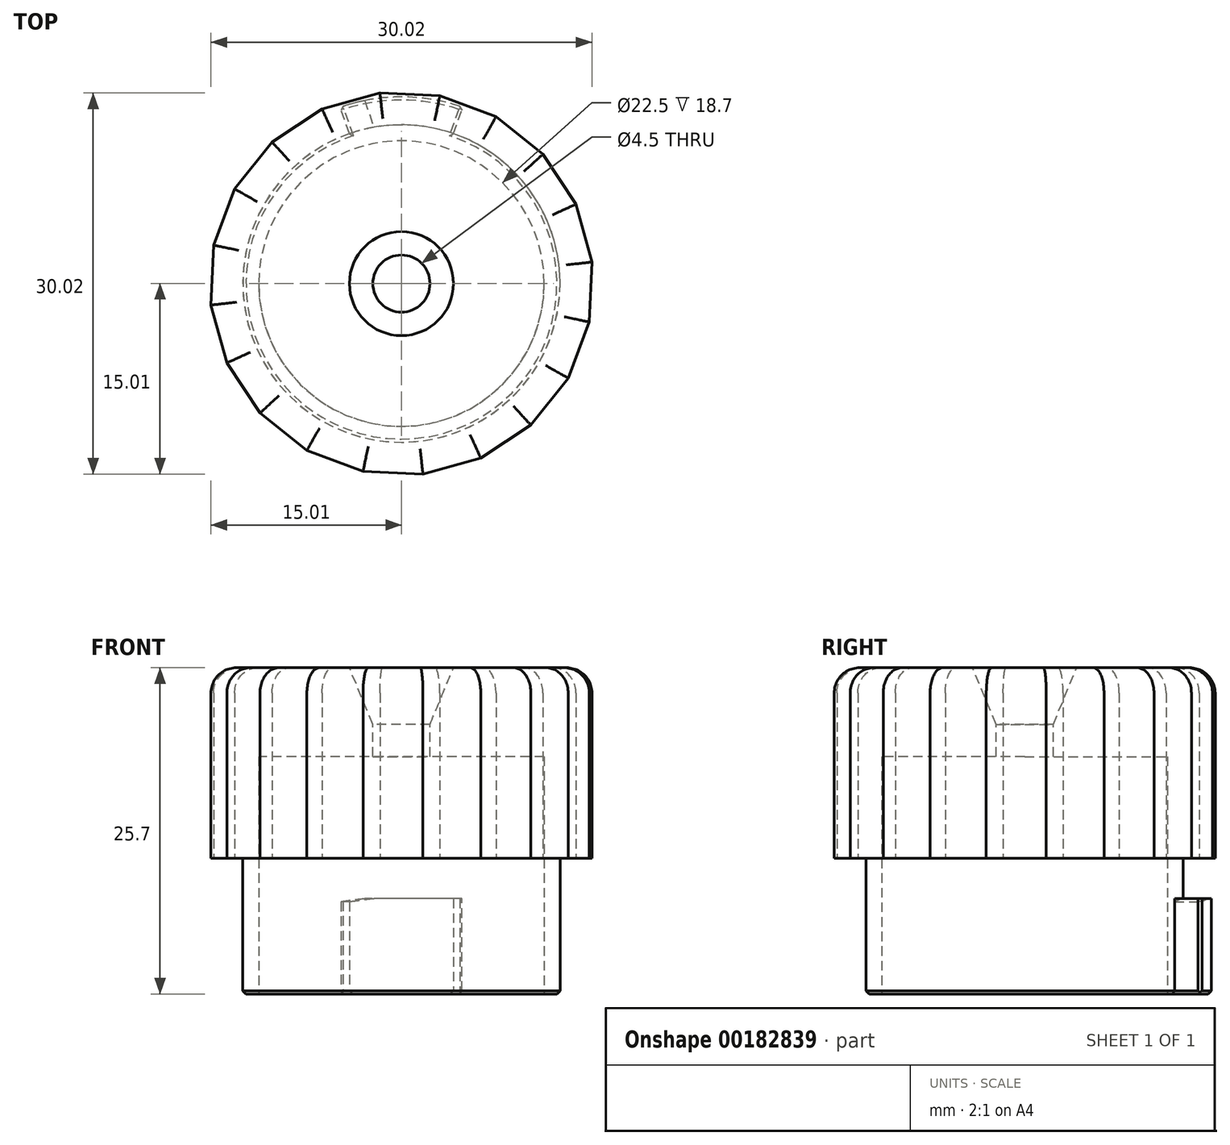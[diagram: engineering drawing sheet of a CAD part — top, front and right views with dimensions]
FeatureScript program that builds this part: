
annotation { "Feature Type Name" : "Feature", "Feature Type Description" : "" }
export const myFeature = defineFeature(function(context is Context, id is Id, definition is map)
    precondition{}
    {
        {
            var Q0;
            Q0=qCreatedBy(makeId("Top.planeOp"),FACE);
            var sketch = newSketch(context, id + "F0", { "sketchPlane" : qUnion([Q0])});
            skLineSegment(sketch, "E0", {"start": v(-4.83, 13.88) * mm, "end": v(-4.1, 11.8) * mm});
            skLineSegment(sketch, "E1", {"start": v(4.83, 13.88) * mm, "end": v(4.1, 11.8) * mm});
            skArc(sketch, "E2", {"start": v(-4.1, 11.8) * mm, "mid": v(0, -12.5) * mm, "end": v(4.1, 11.8) * mm});
            skArc(sketch, "E3", {"start": v(4.83, 13.88) * mm, "mid": v(0, 14.7) * mm, "end": v(-4.83, 13.88) * mm});
            skSolve(sketch);
        }
        {
            var Q0;
            Q0=makeQuery(id+"F0.imprint","IMPRINT",FACE,{"disambiguationData":[TD([[makeQuery(id+"F0.imprint","IMPRINT",EDGE,{"derivedFrom":sQuery(id+"F0.wireOp",EDGE,"E0")}),1.0]])]});
            extrude(context, id + "F1", {"entities" : qUnion([Q0]), "depth" : 7.5 * mm});
        }
        {
            var Q0;
            Q0=makeQuery(id+"F1.opExtrude","CAP_FACE",FACE,{"disambiguationData":[OSD([sQuery(id+"F0.wireOp",EDGE,"E0"),sQuery(id+"F0.wireOp",EDGE,"E1"),sQuery(id+"F0.wireOp",EDGE,"E2"),sQuery(id+"F0.wireOp",EDGE,"E3")])],"isStart":false});
            var sketch = newSketch(context, id + "F2", { "sketchPlane" : qUnion([Q0])});
            skCircle(sketch, "E4", {"center": v(0, 0) * mm, "radius": 12.5 * mm});
            skSolve(sketch);
        }
        {
            var Q0;
            Q0 = qSketchRegion(id + "F2", true);
            extrude(context, id + "F3", {"entities" : qUnion([Q0]), "operationType" : NewBodyOperationType.ADD, "depth" : 3.2 * mm});
        }
        {
            var Q0;
            Q0=makeQuery(id+"F3.opExtrude","CAP_FACE",FACE,{"disambiguationData":[OSD([sQuery(id+"F2.wireOp",EDGE,"E4")])],"isStart":false});
            var sketch = newSketch(context, id + "F4", { "sketchPlane" : qUnion([Q0])});
            skCircle(sketch, "E5.cCircle", {"center": v(0, 0) * mm, "radius": 14.92 * mm, "construction": true});
            skLineSegment(sketch, "E5.0", {"start": v(11.15, 10.2) * mm, "end": v(13.75, 6.25) * mm});
            skLineSegment(sketch, "E5.1", {"start": v(13.75, 6.25) * mm, "end": v(15.01, 1.7) * mm});
            skLineSegment(sketch, "E5.2", {"start": v(15.01, 1.7) * mm, "end": v(14.8, -3.03) * mm});
            skLineSegment(sketch, "E5.3", {"start": v(14.8, -3.03) * mm, "end": v(13.14, -7.45) * mm});
            skLineSegment(sketch, "E5.4", {"start": v(13.14, -7.45) * mm, "end": v(10.2, -11.15) * mm});
            skLineSegment(sketch, "E5.5", {"start": v(10.2, -11.15) * mm, "end": v(6.25, -13.75) * mm});
            skLineSegment(sketch, "E5.6", {"start": v(6.25, -13.75) * mm, "end": v(1.7, -15.01) * mm});
            skLineSegment(sketch, "E5.7", {"start": v(1.7, -15.01) * mm, "end": v(-3.03, -14.8) * mm});
            skLineSegment(sketch, "E5.8", {"start": v(-3.03, -14.8) * mm, "end": v(-7.45, -13.14) * mm});
            skLineSegment(sketch, "E5.9", {"start": v(-7.45, -13.14) * mm, "end": v(-11.15, -10.2) * mm});
            skLineSegment(sketch, "E5.10", {"start": v(-11.15, -10.2) * mm, "end": v(-13.75, -6.25) * mm});
            skLineSegment(sketch, "E5.11", {"start": v(-13.75, -6.25) * mm, "end": v(-15.01, -1.7) * mm});
            skLineSegment(sketch, "E5.12", {"start": v(-15.01, -1.7) * mm, "end": v(-14.8, 3.03) * mm});
            skLineSegment(sketch, "E5.13", {"start": v(-14.8, 3.03) * mm, "end": v(-13.14, 7.45) * mm});
            skLineSegment(sketch, "E5.14", {"start": v(-13.14, 7.45) * mm, "end": v(-10.2, 11.15) * mm});
            skLineSegment(sketch, "E5.15", {"start": v(-10.2, 11.15) * mm, "end": v(-6.25, 13.75) * mm});
            skLineSegment(sketch, "E5.16", {"start": v(-6.25, 13.75) * mm, "end": v(-1.7, 15.01) * mm});
            skLineSegment(sketch, "E5.17", {"start": v(-1.7, 15.01) * mm, "end": v(3.03, 14.8) * mm});
            skLineSegment(sketch, "E5.18", {"start": v(3.03, 14.8) * mm, "end": v(7.45, 13.14) * mm});
            skLineSegment(sketch, "E5.19", {"start": v(7.45, 13.14) * mm, "end": v(11.15, 10.2) * mm});
            skPoint(sketch, "E5.0.midPoint", {"position": v(12.45, 8.22) * mm});
            skSolve(sketch);
        }
        {
            var Q0;
            Q0=makeQuery(id+"F1.opExtrude","CAP_FACE",FACE,{"disambiguationData":[OSD([sQuery(id+"F0.wireOp",EDGE,"E0"),sQuery(id+"F0.wireOp",EDGE,"E1"),sQuery(id+"F0.wireOp",EDGE,"E2"),sQuery(id+"F0.wireOp",EDGE,"E3")])],"isStart":true});
            var sketch = newSketch(context, id + "F5", { "sketchPlane" : qUnion([Q0])});
            skCircle(sketch, "E6", {"center": v(0, 0) * mm, "radius": 11.25 * mm});
            skSolve(sketch);
        }
        {
            var Q0;
            Q0 = qSketchRegion(id + "F5", true);
            extrude(context, id + "F6", {"entities" : qUnion([Q0]), "operationType" : NewBodyOperationType.REMOVE, "oppositeDirection" : true, "depth" : 23 * mm});
        }
        {
            var Q0;
            Q0=makeQuery(id+"F1.opExtrude","SWEPT_EDGE",EDGE,{"disambiguationData":[OSD([sQuery(id+"F0.wireOp",EDGE,"E1"),sQuery(id+"F0.wireOp",EDGE,"E3")])]});
            var Q1;
            Q1=makeQuery(id+"F1.opExtrude","SWEPT_EDGE",EDGE,{"disambiguationData":[OSD([sQuery(id+"F0.wireOp",EDGE,"E0"),sQuery(id+"F0.wireOp",EDGE,"E3")])]});
            chamfer(context, id + "F7", {"entities" : qUnion([Q0, Q1]), "width" : .25 * mm, "tangentPropagation" : true});
        }
        {
            var Q0;
            Q0 = qSketchRegion(id + "F4", true);
            extrude(context, id + "F8", {"entities" : qUnion([Q0]), "operationType" : NewBodyOperationType.ADD, "depth" : 15 * mm});
        }
        {
            var Q0;
            Q0=makeQuery(id+"F8.opExtrude","CAP_FACE",FACE,{"disambiguationData":[OSD([sQuery(id+"F4.wireOp",EDGE,"E5.0"),sQuery(id+"F4.wireOp",EDGE,"E5.1"),sQuery(id+"F4.wireOp",EDGE,"E5.2"),sQuery(id+"F4.wireOp",EDGE,"E5.3"),sQuery(id+"F4.wireOp",EDGE,"E5.4"),sQuery(id+"F4.wireOp",EDGE,"E5.5"),sQuery(id+"F4.wireOp",EDGE,"E5.6"),sQuery(id+"F4.wireOp",EDGE,"E5.7"),sQuery(id+"F4.wireOp",EDGE,"E5.8"),sQuery(id+"F4.wireOp",EDGE,"E5.9"),sQuery(id+"F4.wireOp",EDGE,"E5.10"),sQuery(id+"F4.wireOp",EDGE,"E5.11"),sQuery(id+"F4.wireOp",EDGE,"E5.12"),sQuery(id+"F4.wireOp",EDGE,"E5.13"),sQuery(id+"F4.wireOp",EDGE,"E5.14"),sQuery(id+"F4.wireOp",EDGE,"E5.15"),sQuery(id+"F4.wireOp",EDGE,"E5.16"),sQuery(id+"F4.wireOp",EDGE,"E5.17"),sQuery(id+"F4.wireOp",EDGE,"E5.18"),sQuery(id+"F4.wireOp",EDGE,"E5.19")])],"isStart":false});
            fillet(context, id + "F9", {"entities" : qUnion([Q0]), "radius" : 2 * mm, "tangentPropagation" : true, "allowEdgeOverflow" : false});
        }
        {
            var Q0;
            Q0=makeQuery(id+"F1.opExtrude","CAP_EDGE",EDGE,{"disambiguationData":[OSD([sQuery(id+"F0.wireOp",EDGE,"E2")])],"isStart":true});
            chamfer(context, id + "F10", {"entities" : qUnion([Q0]), "width" : .25 * mm, "tangentPropagation" : true});
        }
        {
            var Q0;
            Q0=makeQuery(id+"F1.opExtrude","CAP_EDGE",EDGE,{"disambiguationData":[OSD([sQuery(id+"F0.wireOp",EDGE,"E0")])],"isStart":true});
            var Q1;
            Q1=makeQuery(id+"F1.opExtrude","CAP_EDGE",EDGE,{"disambiguationData":[OSD([sQuery(id+"F0.wireOp",EDGE,"E3")])],"isStart":true});
            var Q2;
            Q2=makeQuery(id+"F1.opExtrude","CAP_EDGE",EDGE,{"disambiguationData":[OSD([sQuery(id+"F0.wireOp",EDGE,"E1")])],"isStart":true});
            chamfer(context, id + "F11", {"entities" : qUnion([Q0, Q1, Q2]), "width" : .25 * mm, "tangentPropagation" : true});
        }
        {
            var Q0;
            Q0=makeQuery(id+"F1.opExtrude","CAP_EDGE",EDGE,{"disambiguationData":[OSD([sQuery(id+"F0.wireOp",EDGE,"E0")])],"isStart":false});
            chamfer(context, id + "F12", {"entities" : qUnion([Q0]), "chamferType" : ChamferType.TWO_OFFSETS, "width1" : .25 * mm, "oppositeDirection" : true, "width2" : 2 * mm, "tangentPropagation" : true});
        }
        {
            var Q0;
            Q0=makeQuery(id+"F8.opExtrude","CAP_FACE",FACE,{"disambiguationData":[OSD([sQuery(id+"F4.wireOp",EDGE,"E5.0"),sQuery(id+"F4.wireOp",EDGE,"E5.1"),sQuery(id+"F4.wireOp",EDGE,"E5.2"),sQuery(id+"F4.wireOp",EDGE,"E5.3"),sQuery(id+"F4.wireOp",EDGE,"E5.4"),sQuery(id+"F4.wireOp",EDGE,"E5.5"),sQuery(id+"F4.wireOp",EDGE,"E5.6"),sQuery(id+"F4.wireOp",EDGE,"E5.7"),sQuery(id+"F4.wireOp",EDGE,"E5.8"),sQuery(id+"F4.wireOp",EDGE,"E5.9"),sQuery(id+"F4.wireOp",EDGE,"E5.10"),sQuery(id+"F4.wireOp",EDGE,"E5.11"),sQuery(id+"F4.wireOp",EDGE,"E5.12"),sQuery(id+"F4.wireOp",EDGE,"E5.13"),sQuery(id+"F4.wireOp",EDGE,"E5.14"),sQuery(id+"F4.wireOp",EDGE,"E5.15"),sQuery(id+"F4.wireOp",EDGE,"E5.16"),sQuery(id+"F4.wireOp",EDGE,"E5.17"),sQuery(id+"F4.wireOp",EDGE,"E5.18"),sQuery(id+"F4.wireOp",EDGE,"E5.19")])],"isStart":false});
            var sketch = newSketch(context, id + "F13", { "sketchPlane" : qUnion([Q0])});
            skPoint(sketch, "E7", {"position": v(0, 0) * mm});
            skSolve(sketch);
        }
        {
            var Q0;
            Q0=makeQuery(id+"F8.boolean.opBoolean","SPLIT",FACE,{"disambiguationData":[TD([makeQuery(id+"F6.boolean.opBoolean","COPY",FACE,{"derivedFrom":makeQuery(id+"F6.opExtrude","SWEPT_FACE",FACE,{"disambiguationData":[OSD([sQuery(id+"F5.wireOp",EDGE,"E6")])]})})])],"derivedFrom":makeQuery(id+"F8.opExtrude","CAP_FACE",FACE,{"disambiguationData":[OSD([sQuery(id+"F4.wireOp",EDGE,"E5.0"),sQuery(id+"F4.wireOp",EDGE,"E5.1"),sQuery(id+"F4.wireOp",EDGE,"E5.2"),sQuery(id+"F4.wireOp",EDGE,"E5.3"),sQuery(id+"F4.wireOp",EDGE,"E5.4"),sQuery(id+"F4.wireOp",EDGE,"E5.5"),sQuery(id+"F4.wireOp",EDGE,"E5.6"),sQuery(id+"F4.wireOp",EDGE,"E5.7"),sQuery(id+"F4.wireOp",EDGE,"E5.8"),sQuery(id+"F4.wireOp",EDGE,"E5.9"),sQuery(id+"F4.wireOp",EDGE,"E5.10"),sQuery(id+"F4.wireOp",EDGE,"E5.11"),sQuery(id+"F4.wireOp",EDGE,"E5.12"),sQuery(id+"F4.wireOp",EDGE,"E5.13"),sQuery(id+"F4.wireOp",EDGE,"E5.14"),sQuery(id+"F4.wireOp",EDGE,"E5.15"),sQuery(id+"F4.wireOp",EDGE,"E5.16"),sQuery(id+"F4.wireOp",EDGE,"E5.17"),sQuery(id+"F4.wireOp",EDGE,"E5.18"),sQuery(id+"F4.wireOp",EDGE,"E5.19")])],"isStart":true})});
            var sketch = newSketch(context, id + "F14", { "sketchPlane" : qUnion([Q0])});
            skCircle(sketch, "E8", {"center": v(0, 0) * mm, "radius": 1 * mm});
            skSolve(sketch);
        }
        {
            var Q0;
            Q0=makeQuery(id+"F14.imprint","IMPRINT",FACE,{"disambiguationData":[TD([[makeQuery(id+"F14.imprint","IMPRINT",EDGE,{"derivedFrom":sQuery(id+"F14.wireOp",EDGE,"E8")}),-1.0]])]});
            extrude(context, id + "F15", {"entities" : qUnion([Q0]), "operationType" : NewBodyOperationType.REMOVE, "oppositeDirection" : true, "depth" : 8 * mm});
        }
        {
            var Q0;
            Q0=sQuery(id+"F13.wireOp",VERTEX,"E7");
            var Q1;
            Q1=makeQuery(id+"F1.opExtrude","SWEPT_BODY",BODY,{"disambiguationData":[OSD([sQuery(id+"F0.wireOp",EDGE,"E0"),sQuery(id+"F0.wireOp",EDGE,"E1"),sQuery(id+"F0.wireOp",EDGE,"E2"),sQuery(id+"F0.wireOp",EDGE,"E3")])]});
            hole(context, id + "F16", {"style" : HoleStyle.C_SINK, "endStyle" : HoleEndStyle.THROUGH, "holeDiameter" : 4.5 * mm, "cSinkDiameter" : 8.2 * mm, "cSinkAngle" : 45 * degree, "startFromSketch" : true, "locations" : qUnion([Q0]), "scope" : qUnion([Q1]), "isTappedThrough" : true});
        }
    });
